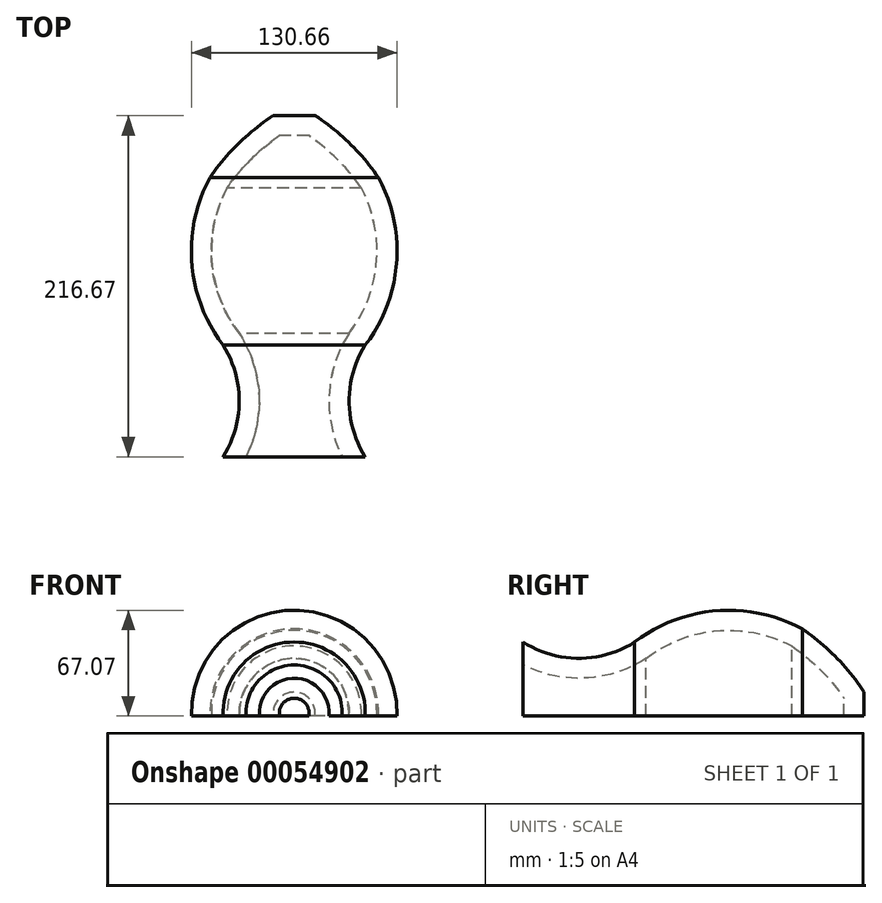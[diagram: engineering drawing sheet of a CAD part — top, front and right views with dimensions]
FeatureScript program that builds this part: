
annotation { "Feature Type Name" : "Feature", "Feature Type Description" : "" }
export const myFeature = defineFeature(function(context is Context, id is Id, definition is map)
    precondition{}
    {
        {
            var Q0;
            Q0=qCreatedBy(makeId("Right.planeOp"),FACE);
            var sketch = newSketch(context, id + "F0", { "sketchPlane" : qUnion([Q0])});
            skLineSegment(sketch, "E0", {"start": v(-108.46, 1.74) * mm, "end": v(115.94, 1.74) * mm});
            skLineSegment(sketch, "E1", {"start": v(-108.46, 1.74) * mm, "end": v(-108.46, 46.88) * mm});
            skArc(sketch, "E2", {"start": v(-108.46, 46.88) * mm, "mid": v(-73, 36.59) * mm, "end": v(-37.53, 46.88) * mm});
            skArc(sketch, "E3", {"start": v(68.87, 55.26) * mm, "mid": v(14.44, 66.77) * mm, "end": v(-37.53, 46.88) * mm});
            skArc(sketch, "E4", {"start": v(115.94, 1.74) * mm, "mid": v(95.75, 31.45) * mm, "end": v(68.87, 55.26) * mm});
            skSolve(sketch);
        }
        {
            var Q0;
            Q0=makeQuery(id+"F0.imprint","IMPRINT",FACE,{"disambiguationData":[TD([[makeQuery(id+"F0.imprint","IMPRINT",EDGE,{"derivedFrom":sQuery(id+"F0.wireOp",EDGE,"E0")}),1.0]])]});
            var Q1;
            Q1=sQuery(id+"F0.wireOp",EDGE,"E0");
            revolve(context, id + "F1", {"entities" : qUnion([Q0]), "axis" : qUnion([Q1]), "revolveType" : RevolveType.FULL});
        }
        {
            var Q0;
            Q0=qCreatedBy(makeId("Right.planeOp"),FACE);
            var sketch = newSketch(context, id + "F2", { "sketchPlane" : qUnion([Q0])});
            skLineSegment(sketch, "E5", {"start": v(108.2, 77.83) * mm, "end": v(108.2, -78.86) * mm});
            skLineSegment(sketch, "E6", {"start": v(108.2, 77.83) * mm, "end": v(126.26, 77.83) * mm});
            skLineSegment(sketch, "E7", {"start": v(126.26, -78.86) * mm, "end": v(108.2, -78.86) * mm});
            skLineSegment(sketch, "E8", {"start": v(126.26, -78.86) * mm, "end": v(126.26, 77.83) * mm});
            skSolve(sketch);
        }
        {
            var Q0;
            Q0 = qSketchRegion(id + "F2", true);
            extrude(context, id + "F3", {"entities" : qUnion([Q0]), "operationType" : NewBodyOperationType.REMOVE, "oppositeDirection" : true, "depth" : 25.4 * mm, "hasSecondDirection" : true, "secondDirectionOppositeDirection" : false, "secondDirectionDepth" : 25.4 * mm});
        }
        {
            var Q0;
            Q0=makeQuery(id+"F1.opRevolve","SWEPT_FACE",FACE,{"disambiguationData":[OSD([sQuery(id+"F0.wireOp",EDGE,"E1")])]});
            shell(context, id + "F4", {"entities" : qUnion([Q0]), "thickness" : 12.7 * mm});
        }
        {
            var Q0;
            Q0=qCreatedBy(makeId("Top.planeOp"),FACE);
            var sketch = newSketch(context, id + "F5", { "sketchPlane" : qUnion([Q0])});
            skLineSegment(sketch, "E9.bottom", {"start": v(-82.5, -115.8) * mm, "end": v(75.32, -115.8) * mm});
            skLineSegment(sketch, "E9.top", {"start": v(-82.5, 113.16) * mm, "end": v(75.32, 113.16) * mm});
            skLineSegment(sketch, "E9.left", {"start": v(-82.5, -115.8) * mm, "end": v(-82.5, 113.16) * mm});
            skLineSegment(sketch, "E9.right", {"start": v(75.32, -115.8) * mm, "end": v(75.32, 113.16) * mm});
            skSolve(sketch);
        }
        {
            var Q0;
            Q0 = qSketchRegion(id + "F5", true);
            extrude(context, id + "F6", {"entities" : qUnion([Q0]), "operationType" : NewBodyOperationType.REMOVE, "oppositeDirection" : true, "depth" : 119.85 * mm});
        }
    });
